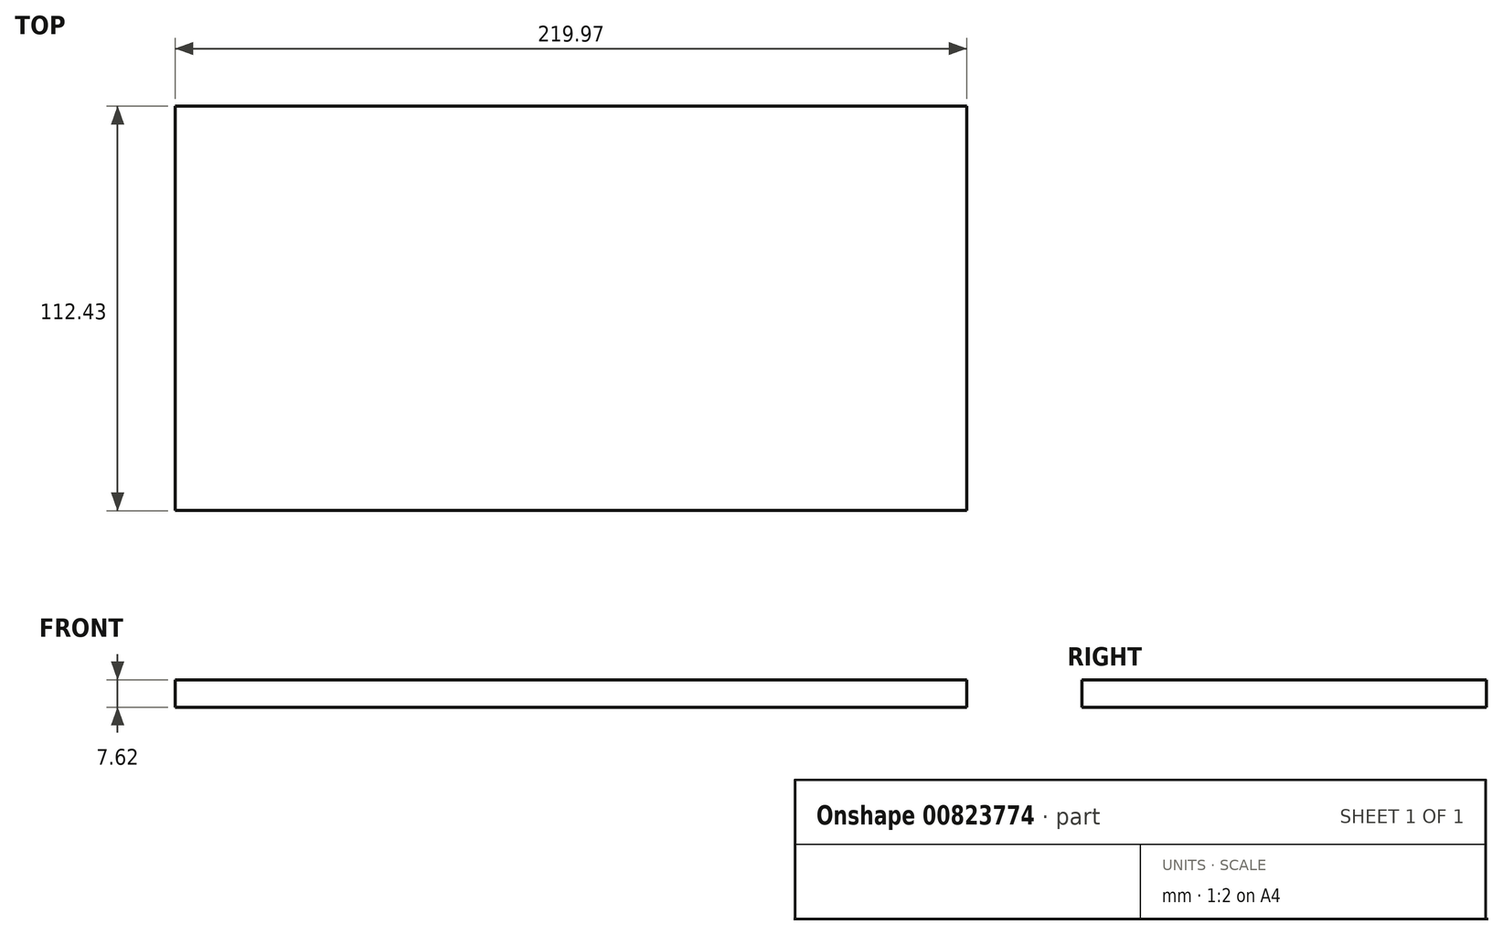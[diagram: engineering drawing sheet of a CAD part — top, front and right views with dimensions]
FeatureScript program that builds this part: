
annotation { "Feature Type Name" : "Feature", "Feature Type Description" : "" }
export const myFeature = defineFeature(function(context is Context, id is Id, definition is map)
    precondition{}
    {
        {
            var Q0;
            Q0=qCreatedBy(makeId("Top.planeOp"),FACE);
            var sketch = newSketch(context, id + "F0", { "sketchPlane" : qUnion([Q0])});
            skLineSegment(sketch, "E0.bottom", {"start": v(75.96, 56.15) * mm, "end": v(-144, 56.15) * mm});
            skLineSegment(sketch, "E0.top", {"start": v(75.96, -56.28) * mm, "end": v(-144, -56.28) * mm});
            skLineSegment(sketch, "E0.left", {"start": v(75.96, 56.15) * mm, "end": v(75.96, -56.28) * mm});
            skLineSegment(sketch, "E0.right", {"start": v(-144, 56.15) * mm, "end": v(-144, -56.28) * mm});
            skSolve(sketch);
        }
        {
            var Q0;
            Q0=makeQuery(id+"F0.imprint","IMPRINT",FACE,{"disambiguationData":[TD([[makeQuery(id+"F0.imprint","IMPRINT",EDGE,{"derivedFrom":sQuery(id+"F0.wireOp",EDGE,"E0.bottom")}),1.0]])]});
            extrude(context, id + "F1", {"entities" : qUnion([Q0]), "depth" : 7.62 * mm, "offsetDistance" : 25.4 * mm});
        }
    });
